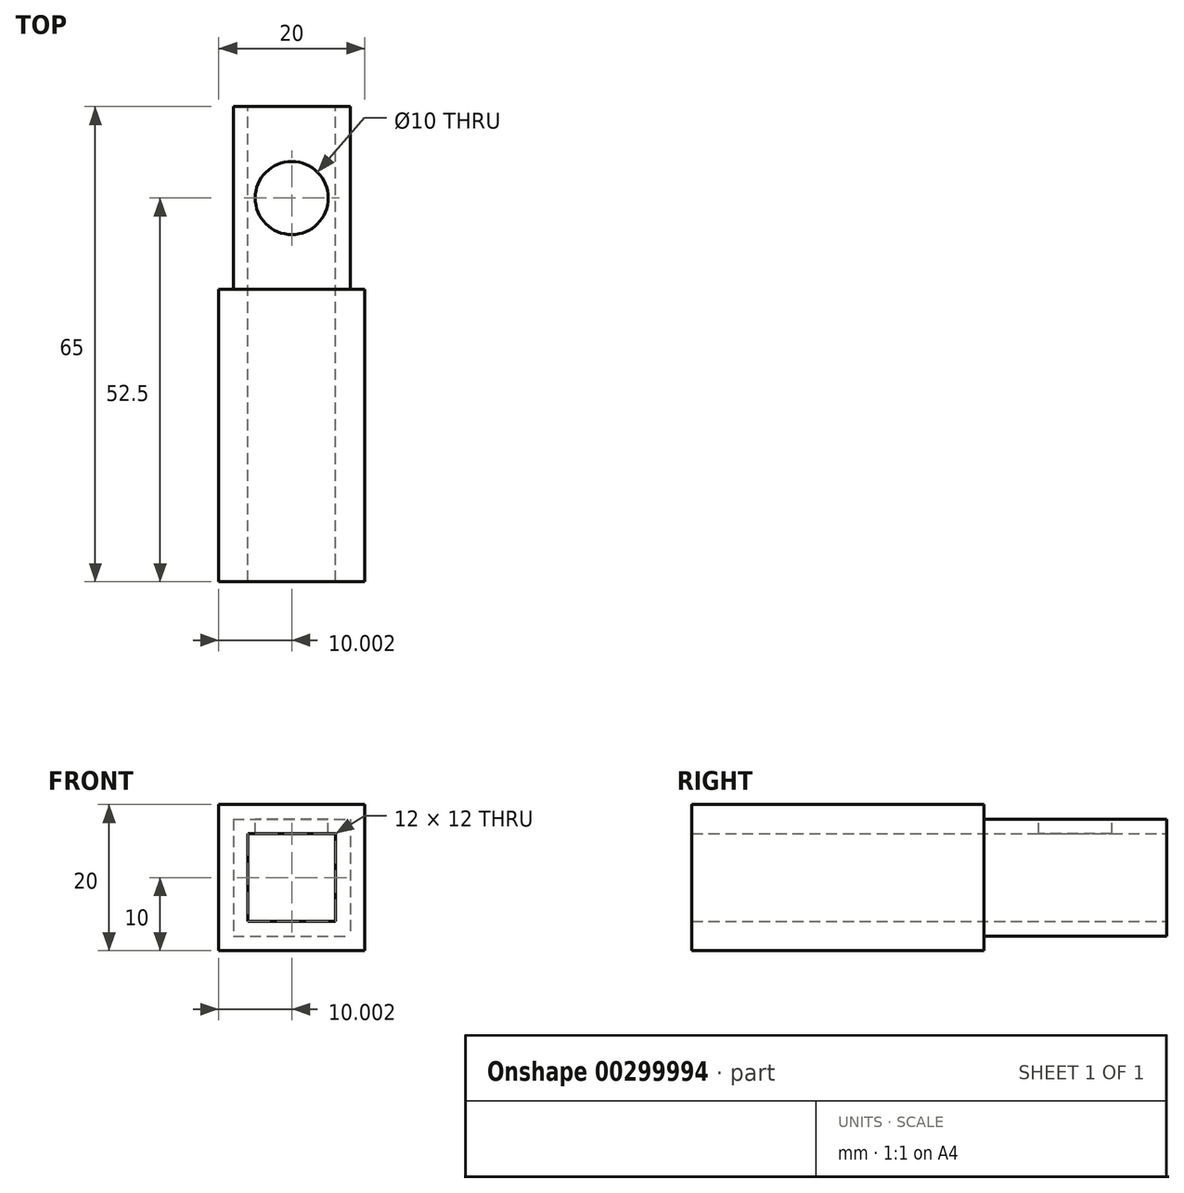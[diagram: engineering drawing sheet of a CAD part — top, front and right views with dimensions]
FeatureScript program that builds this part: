
annotation { "Feature Type Name" : "Feature", "Feature Type Description" : "" }
export const myFeature = defineFeature(function(context is Context, id is Id, definition is map)
    precondition{}
    {
        {
            var Q0;
            Q0=qCreatedBy(makeId("Front.planeOp"),FACE);
            var sketch = newSketch(context, id + "F0", { "sketchPlane" : qUnion([Q0])});
            skLineSegment(sketch, "E0.bottom", {"start": v(5.52, -3.6) * mm, "end": v(21.52, -3.6) * mm});
            skLineSegment(sketch, "E0.top", {"start": v(5.52, -19.6) * mm, "end": v(21.52, -19.6) * mm});
            skLineSegment(sketch, "E0.left", {"start": v(5.52, -3.6) * mm, "end": v(5.52, -19.6) * mm});
            skLineSegment(sketch, "E0.right", {"start": v(21.52, -3.6) * mm, "end": v(21.52, -19.6) * mm});
            skSolve(sketch);
        }
        {
            var Q0;
            Q0 = qSketchRegion(id + "F0", true);
            var Q1;
            Q1=makeQuery(id+"F0.imprint","IMPRINT",FACE,{"disambiguationData":[TD([[makeQuery(id+"F0.imprint","IMPRINT",EDGE,{"derivedFrom":sQuery(id+"F0.wireOp",EDGE,"E0.bottom")}),-1.0]])]});
            extrude(context, id + "F1", {"entities" : qUnion([Q0, Q1]), "depth" : 25 * mm});
        }
        {
            var Q0;
            Q0=makeQuery(id+"F1.opExtrude","CAP_FACE",FACE,{"disambiguationData":[OSD([sQuery(id+"F0.wireOp",EDGE,"E0.bottom"),sQuery(id+"F0.wireOp",EDGE,"E0.top"),sQuery(id+"F0.wireOp",EDGE,"E0.left"),sQuery(id+"F0.wireOp",EDGE,"E0.right")])],"isStart":true});
            var sketch = newSketch(context, id + "F2", { "sketchPlane" : qUnion([Q0])});
            skLineSegment(sketch, "E1.bottom", {"start": v(-7.52, -5.6) * mm, "end": v(-19.52, -5.6) * mm});
            skLineSegment(sketch, "E1.top", {"start": v(-7.52, -17.6) * mm, "end": v(-19.52, -17.6) * mm});
            skLineSegment(sketch, "E1.left", {"start": v(-7.52, -5.6) * mm, "end": v(-7.52, -17.6) * mm});
            skLineSegment(sketch, "E1.right", {"start": v(-19.52, -5.6) * mm, "end": v(-19.52, -17.6) * mm});
            skPoint(sketch, "E1.middle", {"position": v(-13.52, -11.6) * mm});
            skPoint(sketch, "E2", {"position": v(-21.52, -11.6) * mm});
            skPoint(sketch, "E3", {"position": v(-13.52, -3.6) * mm});
            skSolve(sketch);
        }
        {
            var Q0;
            Q0=makeQuery(id+"F2.imprint","IMPRINT",FACE,{"disambiguationData":[TD([[makeQuery(id+"F2.imprint","IMPRINT",EDGE,{"derivedFrom":sQuery(id+"F2.wireOp",EDGE,"E1.bottom")}),1.0]])]});
            extrude(context, id + "F3", {"entities" : qUnion([Q0]), "operationType" : NewBodyOperationType.REMOVE, "oppositeDirection" : true, "depth" : 25 * mm});
        }
        {
            var Q0;
            Q0=makeQuery(id+"F1.opExtrude","CAP_FACE",FACE,{"disambiguationData":[OSD([sQuery(id+"F0.wireOp",EDGE,"E0.bottom"),sQuery(id+"F0.wireOp",EDGE,"E0.top"),sQuery(id+"F0.wireOp",EDGE,"E0.left"),sQuery(id+"F0.wireOp",EDGE,"E0.right")])],"isStart":false});
            var sketch = newSketch(context, id + "F4", { "sketchPlane" : qUnion([Q0])});
            skLineSegment(sketch, "E4.bottom", {"start": v(23.52, -21.6) * mm, "end": v(3.52, -21.6) * mm});
            skLineSegment(sketch, "E4.top", {"start": v(23.52, -1.6) * mm, "end": v(3.52, -1.6) * mm});
            skLineSegment(sketch, "E4.left", {"start": v(23.52, -21.6) * mm, "end": v(23.52, -1.6) * mm});
            skLineSegment(sketch, "E4.right", {"start": v(3.52, -21.6) * mm, "end": v(3.52, -1.6) * mm});
            skPoint(sketch, "E4.middle", {"position": v(13.52, -11.6) * mm});
            skPoint(sketch, "E4.middle.positionSnap0", {"position": v(7.52, -11.6) * mm});
            skPoint(sketch, "E4.middle.positionSnap1", {"position": v(13.52, -3.6) * mm});
            skPoint(sketch, "E4.centerSnap0", {"position": v(7.52, -11.6) * mm});
            skPoint(sketch, "E4.centerSnap1", {"position": v(13.52, -3.6) * mm});
            skSolve(sketch);
        }
        {
            var Q0;
            Q0 = qSketchRegion(id + "F4", true);
            extrude(context, id + "F5", {"entities" : qUnion([Q0]), "operationType" : NewBodyOperationType.ADD, "depth" : 40 * mm});
        }
        {
            var Q0;
            Q0=makeQuery(id+"F1.opExtrude","SWEPT_FACE",FACE,{"disambiguationData":[OSD([sQuery(id+"F0.wireOp",EDGE,"E0.bottom")])]});
            var sketch = newSketch(context, id + "F6", { "sketchPlane" : qUnion([Q0])});
            skCircle(sketch, "E5", {"center": v(13.52, -12.5) * mm, "radius": 5 * mm});
            skPoint(sketch, "E5.centerSnap0", {"position": v(21.52, -12.5) * mm});
            skPoint(sketch, "E5.centerSnap1", {"position": v(13.52, 0) * mm});
            skSolve(sketch);
        }
        {
            var Q0;
            Q0=makeQuery(id+"F6.imprint","IMPRINT",FACE,{"disambiguationData":[TD([[makeQuery(id+"F6.imprint","IMPRINT",EDGE,{"derivedFrom":sQuery(id+"F6.wireOp",EDGE,"E5")}),1.0]])]});
            extrude(context, id + "F7", {"entities" : qUnion([Q0]), "operationType" : NewBodyOperationType.REMOVE, "endBound" : BoundingType.UP_TO_NEXT, "oppositeDirection" : true, "depth" : 25 * mm});
        }
        {
            var Q0;
            Q0=makeQuery(id+"F5.boolean.opBoolean","SPLIT",FACE,{"disambiguationData":[TD([makeQuery(id+"F3.boolean.opBoolean","COPY",FACE,{"derivedFrom":makeQuery(id+"F3.opExtrude","SWEPT_FACE",FACE,{"disambiguationData":[OSD([sQuery(id+"F2.wireOp",EDGE,"E1.bottom")])]})})])],"derivedFrom":makeQuery(id+"F5.opExtrude","CAP_FACE",FACE,{"disambiguationData":[OSD([sQuery(id+"F4.wireOp",EDGE,"E4.bottom"),sQuery(id+"F4.wireOp",EDGE,"E4.top"),sQuery(id+"F4.wireOp",EDGE,"E4.left"),sQuery(id+"F4.wireOp",EDGE,"E4.right")])],"isStart":true})});
            var sketch = newSketch(context, id + "F8", { "sketchPlane" : qUnion([Q0])});
            skLineSegment(sketch, "E6.bottom", {"start": v(-19.52, -17.6) * mm, "end": v(-7.52, -17.6) * mm});
            skLineSegment(sketch, "E6.top", {"start": v(-19.52, -5.6) * mm, "end": v(-7.52, -5.6) * mm});
            skLineSegment(sketch, "E6.left", {"start": v(-19.52, -17.6) * mm, "end": v(-19.52, -5.6) * mm});
            skLineSegment(sketch, "E6.right", {"start": v(-7.52, -17.6) * mm, "end": v(-7.52, -5.6) * mm});
            skPoint(sketch, "E6.middle", {"position": v(-13.52, -11.6) * mm});
            skPoint(sketch, "E6.middle.positionSnap0", {"position": v(-13.52, -5.6) * mm});
            skPoint(sketch, "E6.middle.positionSnap1", {"position": v(-7.52, -11.6) * mm});
            skPoint(sketch, "E6.centerSnap0", {"position": v(-13.52, -5.6) * mm});
            skPoint(sketch, "E6.centerSnap1", {"position": v(-7.52, -11.6) * mm});
            skSolve(sketch);
        }
        {
            var Q0;
            Q0=makeQuery(id+"F8.imprint","IMPRINT",FACE,{"disambiguationData":[TD([[makeQuery(id+"F8.imprint","IMPRINT",EDGE,{"derivedFrom":sQuery(id+"F8.wireOp",EDGE,"E6.bottom")}),-1.0]])]});
            extrude(context, id + "F9", {"entities" : qUnion([Q0]), "operationType" : NewBodyOperationType.REMOVE, "endBound" : BoundingType.UP_TO_NEXT, "oppositeDirection" : true, "depth" : 25 * mm});
        }
    });
